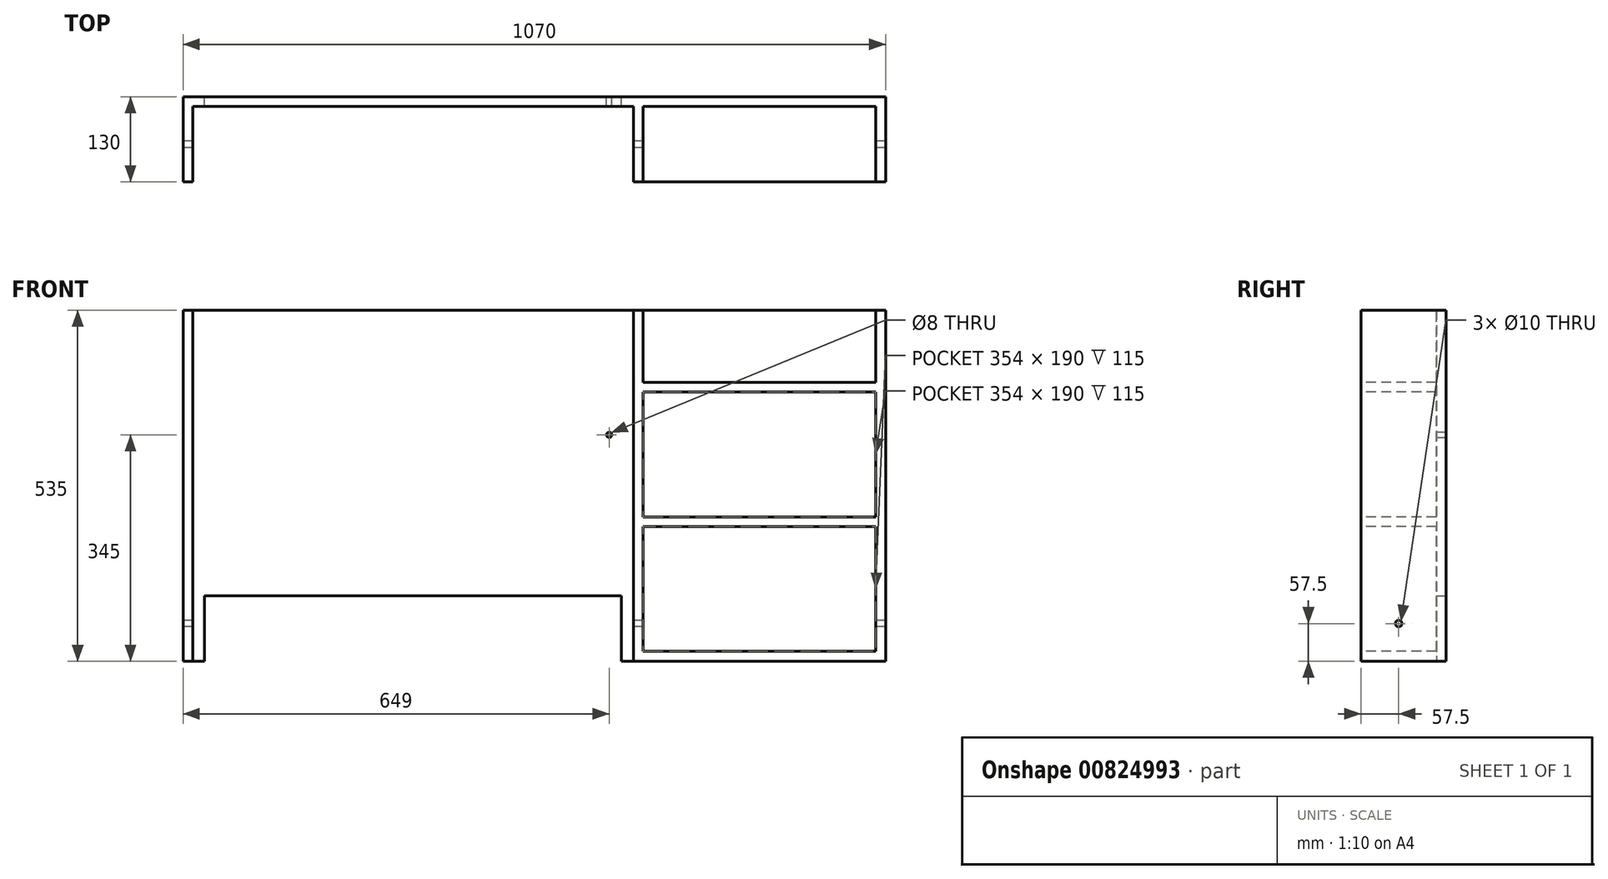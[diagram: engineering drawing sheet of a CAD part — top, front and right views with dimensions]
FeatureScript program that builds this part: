
annotation { "Feature Type Name" : "Feature", "Feature Type Description" : "" }
export const myFeature = defineFeature(function(context is Context, id is Id, definition is map)
    precondition{}
    {
        {
            var Q0;
            Q0=qCreatedBy(makeId("Front.planeOp"),FACE);
            var sketch = newSketch(context, id + "F0", { "sketchPlane" : qUnion([Q0])});
            skLineSegment(sketch, "E0.bottom", {"start": v(0, 553) * mm, "end": v(701, 553) * mm});
            skLineSegment(sketch, "E0.top", {"start": v(0, 0) * mm, "end": v(701, 0) * mm});
            skLineSegment(sketch, "E0.left", {"start": v(0, 553) * mm, "end": v(0, 0) * mm});
            skLineSegment(sketch, "E0.right", {"start": v(701, 553) * mm, "end": v(701, 0) * mm});
            skSolve(sketch);
        }
        {
            var Q0;
            Q0=makeQuery(id+"F0.imprint","IMPRINT",FACE,{"disambiguationData":[TD([[makeQuery(id+"F0.imprint","IMPRINT",EDGE,{"derivedFrom":sQuery(id+"F0.wireOp",EDGE,"E0.bottom")}),-1.0]])]});
            extrude(context, id + "F1", {"entities" : qUnion([Q0]), "oppositeDirection" : true, "depth" : 15 * mm, "offsetDistance" : 25 * mm});
        }
        {
            var Q0;
            Q0=makeQuery(id+"F0.imprint","IMPRINT",FACE,{"disambiguationData":[TD([[makeQuery(id+"F0.imprint","IMPRINT",EDGE,{"derivedFrom":sQuery(id+"F0.wireOp",EDGE,"E0.bottom")}),-1.0]])]});
            var sketch = newSketch(context, id + "F2", { "sketchPlane" : qUnion([Q0])});
            skLineSegment(sketch, "E1.bottom", {"start": v(0, 0) * mm, "end": v(15, 0) * mm});
            skLineSegment(sketch, "E1.left", {"start": v(0, 0) * mm, "end": v(0, 553) * mm});
            skLineSegment(sketch, "E1.right", {"start": v(15, 0) * mm, "end": v(15, 538) * mm});
            skLineSegment(sketch, "E2.bottom", {"start": v(0, 553) * mm, "end": v(701, 553) * mm});
            skLineSegment(sketch, "E2.top", {"start": v(15, 538) * mm, "end": v(686, 538) * mm});
            skLineSegment(sketch, "E3.top", {"start": v(701, 0) * mm, "end": v(686, 0) * mm});
            skLineSegment(sketch, "E3.left", {"start": v(701, 553) * mm, "end": v(701, 0) * mm});
            skLineSegment(sketch, "E3.right", {"start": v(686, 538) * mm, "end": v(686, 0) * mm});
            skSolve(sketch);
        }
        {
            var Q0;
            Q0=makeQuery(id+"F2.imprint","IMPRINT",FACE,{"disambiguationData":[TD([[makeQuery(id+"F2.imprint","IMPRINT",EDGE,{"derivedFrom":sQuery(id+"F2.wireOp",EDGE,"E1.bottom")}),1.0]])]});
            extrude(context, id + "F3", {"entities" : qUnion([Q0]), "operationType" : NewBodyOperationType.ADD, "depth" : 115 * mm, "offsetDistance" : 25 * mm});
        }
        {
            var Q0;
            Q0=makeQuery(id+"F3.boolean.opBoolean","MERGE",FACE,{"derivedFrom":[makeQuery(id+"F1.opExtrude","SWEPT_FACE",FACE,{"disambiguationData":[OSD([sQuery(id+"F0.wireOp",EDGE,"E0.left")])]}),makeQuery(id+"F3.opExtrude","SWEPT_FACE",FACE,{"disambiguationData":[OSD([sQuery(id+"F2.wireOp",EDGE,"E1.left")])]})]});
            var sketch = newSketch(context, id + "F4", { "sketchPlane" : qUnion([Q0])});
            skPoint(sketch, "E4", {"position": v(57.5, 57.5) * mm});
            skSolve(sketch);
        }
        {
            var Q0;
            Q0=sQuery(id+"F4.wireOp",VERTEX,"E4");
            var Q1;
            Q1=makeQuery(id+"F1.opExtrude","SWEPT_BODY",BODY,{"disambiguationData":[OSD([sQuery(id+"F0.wireOp",EDGE,"E0.bottom"),sQuery(id+"F0.wireOp",EDGE,"E0.top"),sQuery(id+"F0.wireOp",EDGE,"E0.left"),sQuery(id+"F0.wireOp",EDGE,"E0.right")])]});
            hole(context, id + "F5", {"style" : HoleStyle.SIMPLE, "endStyle" : HoleEndStyle.THROUGH, "holeDiameter" : 10 * mm, "majorDiameter" : 5 * mm, "isTappedThrough" : true, "tappedDepth" : 12 * mm, "tapClearance" : 3, "startFromSketch" : true, "locations" : qUnion([Q0]), "scope" : qUnion([Q1])});
        }
        {
            var Q0;
            Q0=makeQuery(id+"F3.boolean.opBoolean","MERGE",FACE,{"derivedFrom":[makeQuery(id+"F1.opExtrude","SWEPT_FACE",FACE,{"disambiguationData":[OSD([sQuery(id+"F0.wireOp",EDGE,"E0.right")])]}),makeQuery(id+"F3.opExtrude","SWEPT_FACE",FACE,{"disambiguationData":[OSD([sQuery(id+"F2.wireOp",EDGE,"E3.left")])]})]});
            var sketch = newSketch(context, id + "F6", { "sketchPlane" : qUnion([Q0])});
            skLineSegment(sketch, "E5.bottom", {"start": v(-115, 553) * mm, "end": v(15, 553) * mm});
            skLineSegment(sketch, "E5.top", {"start": v(-115, 0) * mm, "end": v(15, 0) * mm});
            skLineSegment(sketch, "E5.left", {"start": v(-115, 553) * mm, "end": v(-115, 0) * mm});
            skLineSegment(sketch, "E5.right", {"start": v(15, 553) * mm, "end": v(15, 0) * mm});
            skSolve(sketch);
        }
        {
            var Q0;
            Q0=makeQuery(id+"F6.imprint","IMPRINT",FACE,{"disambiguationData":[TD([[makeQuery(id+"F6.imprint","IMPRINT",EDGE,{"derivedFrom":sQuery(id+"F6.wireOp",EDGE,"E5.bottom")}),1.0]])]});
            extrude(context, id + "F7", {"entities" : qUnion([Q0]), "operationType" : NewBodyOperationType.ADD, "depth" : 369 * mm, "offsetDistance" : 25 * mm});
        }
        {
            var Q0;
            Q0=makeQuery(id+"F7.boolean.opBoolean","MERGE",FACE,{"derivedFrom":[makeQuery(id+"F3.opExtrude","CAP_FACE",FACE,{"disambiguationData":[OSD([sQuery(id+"F2.wireOp",EDGE,"E1.bottom"),sQuery(id+"F2.wireOp",EDGE,"E1.left"),sQuery(id+"F2.wireOp",EDGE,"E1.right"),sQuery(id+"F2.wireOp",EDGE,"E2.bottom"),sQuery(id+"F2.wireOp",EDGE,"E2.top"),sQuery(id+"F2.wireOp",EDGE,"E3.top"),sQuery(id+"F2.wireOp",EDGE,"E3.left"),sQuery(id+"F2.wireOp",EDGE,"E3.right")])],"isStart":false}),makeQuery(id+"F7.opExtrude","SWEPT_FACE",FACE,{"disambiguationData":[OSD([sQuery(id+"F6.wireOp",EDGE,"E5.left")])]})]});
            var sketch = newSketch(context, id + "F8", { "sketchPlane" : qUnion([Q0])});
            skLineSegment(sketch, "E6.bottom", {"start": v(701, 538) * mm, "end": v(1055, 538) * mm});
            skLineSegment(sketch, "E6.top", {"start": v(701, 425) * mm, "end": v(1055, 425) * mm});
            skLineSegment(sketch, "E6.left", {"start": v(701, 538) * mm, "end": v(701, 425) * mm});
            skLineSegment(sketch, "E6.right", {"start": v(1055, 538) * mm, "end": v(1055, 425) * mm});
            skLineSegment(sketch, "E7.bottom", {"start": v(701, 410) * mm, "end": v(1055, 410) * mm});
            skLineSegment(sketch, "E7.top", {"start": v(701, 220) * mm, "end": v(1055, 220) * mm});
            skLineSegment(sketch, "E7.left", {"start": v(701, 410) * mm, "end": v(701, 220) * mm});
            skLineSegment(sketch, "E7.right", {"start": v(1055, 410) * mm, "end": v(1055, 220) * mm});
            skLineSegment(sketch, "E8.bottom", {"start": v(701, 205) * mm, "end": v(1055, 205) * mm});
            skLineSegment(sketch, "E8.top", {"start": v(701, 15) * mm, "end": v(1055, 15) * mm});
            skLineSegment(sketch, "E8.left", {"start": v(701, 205) * mm, "end": v(701, 15) * mm});
            skLineSegment(sketch, "E8.right", {"start": v(1055, 205) * mm, "end": v(1055, 15) * mm});
            skSolve(sketch);
        }
        {
            var Q0;
            Q0=makeQuery(id+"F8.imprint","IMPRINT",FACE,{"disambiguationData":[TD([[makeQuery(id+"F8.imprint","IMPRINT",EDGE,{"derivedFrom":sQuery(id+"F8.wireOp",EDGE,"E6.bottom")}),-1.0]])]});
            var Q1;
            Q1=makeQuery(id+"F8.imprint","IMPRINT",FACE,{"disambiguationData":[TD([[makeQuery(id+"F8.imprint","IMPRINT",EDGE,{"derivedFrom":sQuery(id+"F8.wireOp",EDGE,"E7.bottom")}),-1.0]])]});
            var Q2;
            Q2=makeQuery(id+"F8.imprint","IMPRINT",FACE,{"disambiguationData":[TD([[makeQuery(id+"F8.imprint","IMPRINT",EDGE,{"derivedFrom":sQuery(id+"F8.wireOp",EDGE,"E8.bottom")}),-1.0]])]});
            extrude(context, id + "F9", {"entities" : qUnion([Q0, Q1, Q2]), "operationType" : NewBodyOperationType.REMOVE, "endBound" : BoundingType.UP_TO_NEXT, "oppositeDirection" : true, "depth" : 25 * mm, "hasOffset" : true, "offsetDistance" : 15 * mm});
        }
        {
            var Q0;
            Q0=makeQuery(id+"F7.boolean.opBoolean","MERGE",FACE,{"derivedFrom":[makeQuery(id+"F3.boolean.opBoolean","MERGE",FACE,{"derivedFrom":[makeQuery(id+"F1.opExtrude","SWEPT_FACE",FACE,{"disambiguationData":[OSD([sQuery(id+"F0.wireOp",EDGE,"E0.bottom")])]}),makeQuery(id+"F3.opExtrude","SWEPT_FACE",FACE,{"disambiguationData":[OSD([sQuery(id+"F2.wireOp",EDGE,"E2.bottom")])]})]}),makeQuery(id+"F7.opExtrude","SWEPT_FACE",FACE,{"disambiguationData":[OSD([sQuery(id+"F6.wireOp",EDGE,"E5.bottom")])]})]});
            var sketch = newSketch(context, id + "F10", { "sketchPlane" : qUnion([Q0])});
            skLineSegment(sketch, "E9.bottom", {"start": v(0, 15) * mm, "end": v(1070, 15) * mm});
            skLineSegment(sketch, "E9.top", {"start": v(0, -115) * mm, "end": v(1070, -115) * mm});
            skLineSegment(sketch, "E9.left", {"start": v(0, 15) * mm, "end": v(0, -115) * mm});
            skLineSegment(sketch, "E9.right", {"start": v(1070, 15) * mm, "end": v(1070, -115) * mm});
            skSolve(sketch);
        }
        {
            var Q0;
            Q0=makeQuery(id+"F10.imprint","IMPRINT",FACE,{"disambiguationData":[TD([[makeQuery(id+"F10.imprint","IMPRINT",EDGE,{"derivedFrom":sQuery(id+"F10.wireOp",EDGE,"E9.bottom")}),-1.0]])]});
            extrude(context, id + "F11", {"entities" : qUnion([Q0]), "operationType" : NewBodyOperationType.REMOVE, "oppositeDirection" : true, "depth" : 18 * mm, "offsetDistance" : 25 * mm});
        }
        {
            var Q0;
            Q0=makeQuery(id+"F7.boolean.opBoolean","MERGE",FACE,{"derivedFrom":[makeQuery(id+"F3.boolean.opBoolean","MERGE",FACE,{"derivedFrom":[makeQuery(id+"F1.opExtrude","SWEPT_FACE",FACE,{"disambiguationData":[OSD([sQuery(id+"F0.wireOp",EDGE,"E0.top")])]}),makeQuery(id+"F3.opExtrude","SWEPT_FACE",FACE,{"disambiguationData":[OSD([sQuery(id+"F2.wireOp",EDGE,"E1.bottom")])]}),makeQuery(id+"F3.opExtrude","SWEPT_FACE",FACE,{"disambiguationData":[OSD([sQuery(id+"F2.wireOp",EDGE,"E3.top")])]})]}),makeQuery(id+"F7.opExtrude","SWEPT_FACE",FACE,{"disambiguationData":[OSD([sQuery(id+"F6.wireOp",EDGE,"E5.top")])]})]});
            var sketch = newSketch(context, id + "F12", { "sketchPlane" : qUnion([Q0])});
            skLineSegment(sketch, "E10.bottom", {"start": v(33, 0) * mm, "end": v(668, 0) * mm});
            skLineSegment(sketch, "E10.top", {"start": v(33, -15) * mm, "end": v(668, -15) * mm});
            skLineSegment(sketch, "E10.left", {"start": v(33, 0) * mm, "end": v(33, -15) * mm});
            skLineSegment(sketch, "E10.right", {"start": v(668, 0) * mm, "end": v(668, -15) * mm});
            skSolve(sketch);
        }
        {
            var Q0;
            Q0=makeQuery(id+"F12.imprint","IMPRINT",FACE,{"disambiguationData":[TD([[makeQuery(id+"F12.imprint","IMPRINT",EDGE,{"derivedFrom":sQuery(id+"F12.wireOp",EDGE,"E10.bottom")}),-1.0]])]});
            extrude(context, id + "F13", {"entities" : qUnion([Q0]), "operationType" : NewBodyOperationType.REMOVE, "oppositeDirection" : true, "depth" : 100 * mm, "offsetDistance" : 25 * mm});
        }
        {
            var Q0;
            Q0=makeQuery(id+"F7.boolean.opBoolean","MERGE",FACE,{"derivedFrom":[makeQuery(id+"F1.opExtrude","CAP_FACE",FACE,{"disambiguationData":[OSD([sQuery(id+"F0.wireOp",EDGE,"E0.bottom"),sQuery(id+"F0.wireOp",EDGE,"E0.top"),sQuery(id+"F0.wireOp",EDGE,"E0.left"),sQuery(id+"F0.wireOp",EDGE,"E0.right")])],"isStart":false}),makeQuery(id+"F7.opExtrude","SWEPT_FACE",FACE,{"disambiguationData":[OSD([sQuery(id+"F6.wireOp",EDGE,"E5.right")])]})]});
            var sketch = newSketch(context, id + "F14", { "sketchPlane" : qUnion([Q0])});
            skPoint(sketch, "E11", {"position": v(-649, 345) * mm});
            skSolve(sketch);
        }
        {
            var Q0;
            Q0=sQuery(id+"F14.wireOp",VERTEX,"E11");
            var Q1;
            Q1=makeQuery(id+"F1.opExtrude","SWEPT_BODY",BODY,{"disambiguationData":[OSD([sQuery(id+"F0.wireOp",EDGE,"E0.bottom"),sQuery(id+"F0.wireOp",EDGE,"E0.top"),sQuery(id+"F0.wireOp",EDGE,"E0.left"),sQuery(id+"F0.wireOp",EDGE,"E0.right")])]});
            hole(context, id + "F15", {"style" : HoleStyle.SIMPLE, "endStyle" : HoleEndStyle.THROUGH, "holeDiameter" : 8 * mm, "majorDiameter" : 5 * mm, "isTappedThrough" : true, "tappedDepth" : 12 * mm, "tapClearance" : 3, "locations" : qUnion([Q0]), "scope" : qUnion([Q1])});
        }
    });
